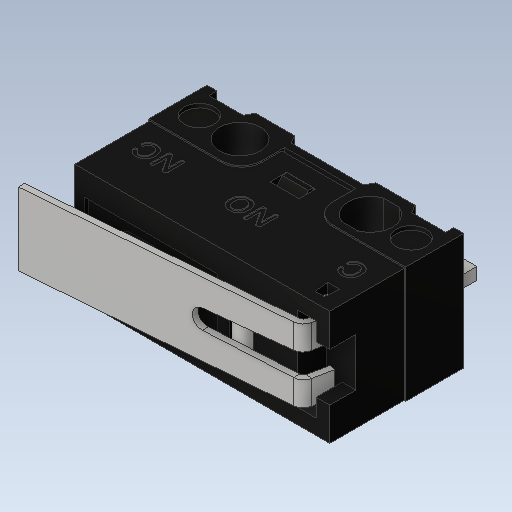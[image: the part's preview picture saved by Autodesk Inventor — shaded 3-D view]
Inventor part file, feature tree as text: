
AUTODESK INVENTOR PART (.ipt)
format: ipt  version: 2020.1 (Build 241239000, 239)  size: 1,117,184 bytes
history: native  units: mm
features: other x3, surface_op x1, extrude x1, sketch x1
ambient origin geometry x8: Origin, YZ Plane, XZ Plane, XY Plane, X Axis, Y Axis, Z Axis, Center Point
bodies: Solid1 (feature_tree), Solid2 (feature_tree)
feature tree (6):
  surface_op  "Sculpt1"
  extrude  "Extrusion1"  [1 undecoded]
  sketch  "Sketch2"  dims[d4=2.0mm d5=0.0mm]
  other  "ZMA00A150L04PC"
  other  "Composite1"
  other  "Srf1"
note: 1 required parameter value undecoded (feature->parameter linkage not recoverable at this tier; creation-order binding heuristic only, values carry confidence <= 0.55)
